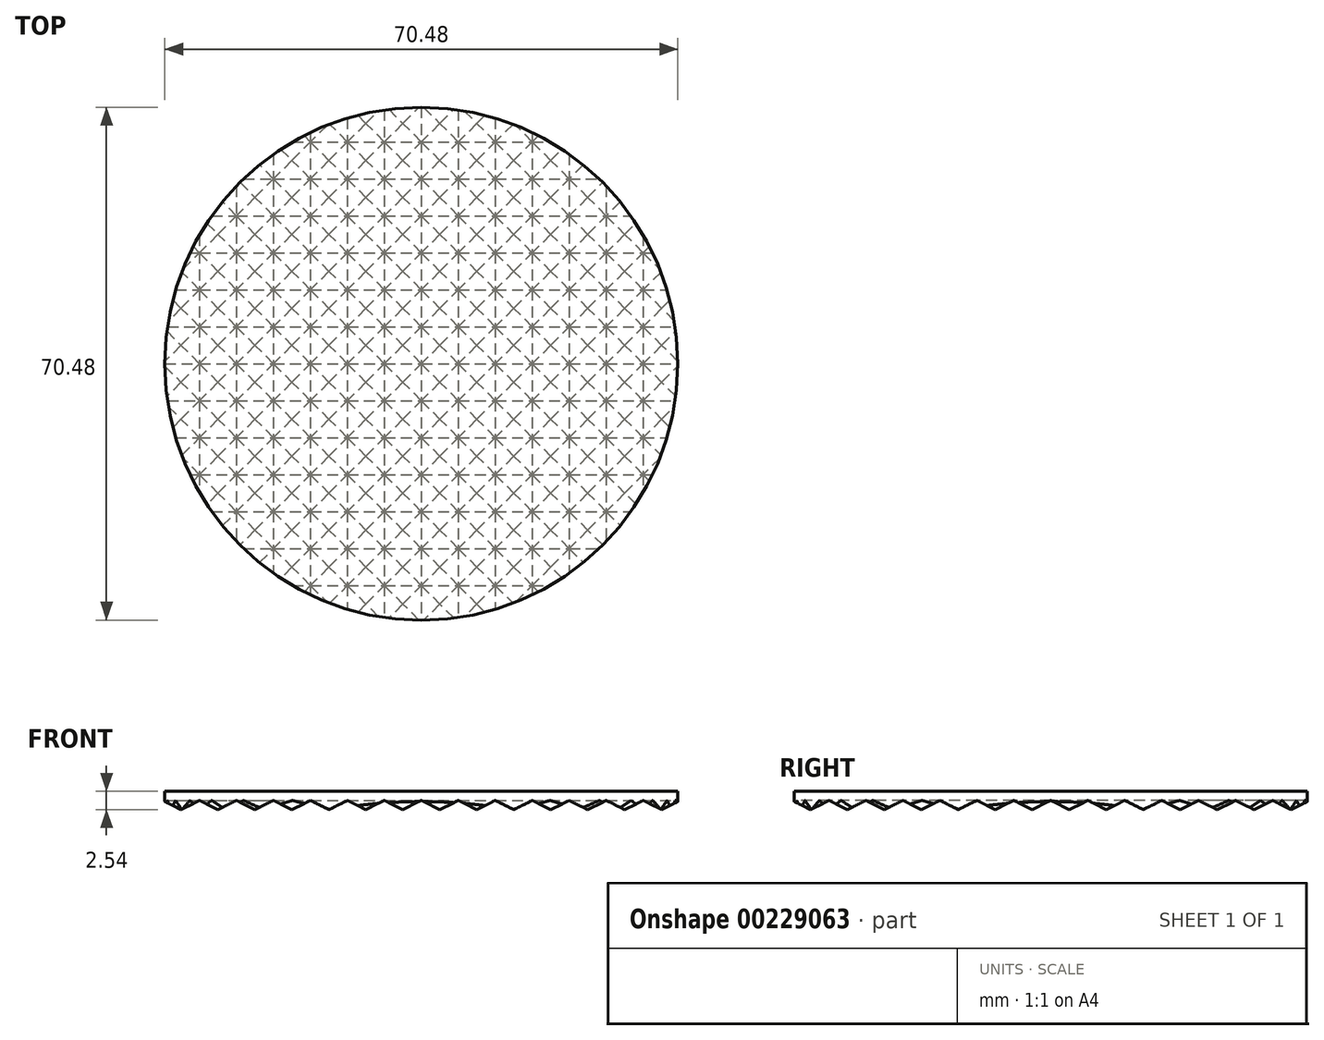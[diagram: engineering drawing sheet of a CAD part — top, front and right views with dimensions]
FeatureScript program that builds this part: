
annotation { "Feature Type Name" : "Feature", "Feature Type Description" : "" }
export const myFeature = defineFeature(function(context is Context, id is Id, definition is map)
    precondition{}
    {
        {
            var Q0;
            Q0=qCreatedBy(makeId("Top.planeOp"),FACE);
            var sketch = newSketch(context, id + "F0", { "sketchPlane" : qUnion([Q0])});
            skCircle(sketch, "E0", {"center": v(0, 0) * mm, "radius": 35.24 * mm});
            skSolve(sketch);
        }
        {
            var Q0;
            Q0 = qSketchRegion(id + "F0", true);
            extrude(context, id + "F1", {"entities" : qUnion([Q0]), "depth" : 2.54 * mm});
        }
        {
            var Q0;
            Q0=qCreatedBy(makeId("Front.planeOp"),FACE);
            var sketch = newSketch(context, id + "F2", { "sketchPlane" : qUnion([Q0])});
            skLineSegment(sketch, "E1", {"start": v(0, 0) * mm, "end": v(-2.54, 0) * mm});
            skLineSegment(sketch, "E2", {"start": v(-2.54, 0) * mm, "end": v(0, 1.27) * mm});
            skLineSegment(sketch, "E3", {"start": v(0, 1.27) * mm, "end": v(2.54, 0) * mm});
            skLineSegment(sketch, "E4", {"start": v(2.54, 0) * mm, "end": v(0, 0) * mm});
            skLineSegment(sketch, "E5.1.0.0", {"start": v(5.08, 1.27) * mm, "end": v(7.62, 0) * mm});
            skLineSegment(sketch, "E5.1.0.1", {"start": v(7.62, 0) * mm, "end": v(5.08, 0) * mm});
            skLineSegment(sketch, "E5.1.0.2", {"start": v(5.08, 0) * mm, "end": v(2.54, 0) * mm});
            skLineSegment(sketch, "E5.1.0.3", {"start": v(2.54, 0) * mm, "end": v(5.08, 1.27) * mm});
            skLineSegment(sketch, "E5.2.0.0", {"start": v(10.16, 1.27) * mm, "end": v(12.7, 0) * mm});
            skLineSegment(sketch, "E5.2.0.1", {"start": v(12.7, 0) * mm, "end": v(10.16, 0) * mm});
            skLineSegment(sketch, "E5.2.0.2", {"start": v(10.16, 0) * mm, "end": v(7.62, 0) * mm});
            skLineSegment(sketch, "E5.2.0.3", {"start": v(7.62, 0) * mm, "end": v(10.16, 1.27) * mm});
            skLineSegment(sketch, "E5.3.0.0", {"start": v(15.24, 1.27) * mm, "end": v(17.78, 0) * mm});
            skLineSegment(sketch, "E5.3.0.1", {"start": v(17.78, 0) * mm, "end": v(15.24, 0) * mm});
            skLineSegment(sketch, "E5.3.0.2", {"start": v(15.24, 0) * mm, "end": v(12.7, 0) * mm});
            skLineSegment(sketch, "E5.3.0.3", {"start": v(12.7, 0) * mm, "end": v(15.24, 1.27) * mm});
            skLineSegment(sketch, "E5.4.0.0", {"start": v(20.32, 1.27) * mm, "end": v(22.86, 0) * mm});
            skLineSegment(sketch, "E5.4.0.1", {"start": v(22.86, 0) * mm, "end": v(20.32, 0) * mm});
            skLineSegment(sketch, "E5.4.0.2", {"start": v(20.32, 0) * mm, "end": v(17.78, 0) * mm});
            skLineSegment(sketch, "E5.4.0.3", {"start": v(17.78, 0) * mm, "end": v(20.32, 1.27) * mm});
            skLineSegment(sketch, "E5.5.0.0", {"start": v(25.4, 1.27) * mm, "end": v(27.94, 0) * mm});
            skLineSegment(sketch, "E5.5.0.1", {"start": v(27.94, 0) * mm, "end": v(25.4, 0) * mm});
            skLineSegment(sketch, "E5.5.0.2", {"start": v(25.4, 0) * mm, "end": v(22.86, 0) * mm});
            skLineSegment(sketch, "E5.5.0.3", {"start": v(22.86, 0) * mm, "end": v(25.4, 1.27) * mm});
            skLineSegment(sketch, "E5.6.0.0", {"start": v(30.48, 1.27) * mm, "end": v(33.02, 0) * mm});
            skLineSegment(sketch, "E5.6.0.1", {"start": v(33.02, 0) * mm, "end": v(30.48, 0) * mm});
            skLineSegment(sketch, "E5.6.0.2", {"start": v(30.48, 0) * mm, "end": v(27.94, 0) * mm});
            skLineSegment(sketch, "E5.6.0.3", {"start": v(27.94, 0) * mm, "end": v(30.48, 1.27) * mm});
            skLineSegment(sketch, "E5.7.0.0", {"start": v(35.56, 1.27) * mm, "end": v(38.1, 0) * mm});
            skLineSegment(sketch, "E5.7.0.1", {"start": v(38.1, 0) * mm, "end": v(35.56, 0) * mm});
            skLineSegment(sketch, "E5.7.0.2", {"start": v(35.56, 0) * mm, "end": v(33.02, 0) * mm});
            skLineSegment(sketch, "E5.7.0.3", {"start": v(33.02, 0) * mm, "end": v(35.56, 1.27) * mm});
            skLineSegment(sketch, "E5.direction1", {"start": v(0, 1.27) * mm, "end": v(5.08, 1.27) * mm, "construction": true});
            skLineSegment(sketch, "E6.1.0.0", {"start": v(-2.54, 0) * mm, "end": v(-5.08, 0) * mm});
            skLineSegment(sketch, "E6.1.0.1", {"start": v(-5.08, 1.27) * mm, "end": v(-2.54, 0) * mm});
            skLineSegment(sketch, "E6.1.0.2", {"start": v(-7.62, 0) * mm, "end": v(-5.08, 1.27) * mm});
            skLineSegment(sketch, "E6.1.0.3", {"start": v(-5.08, 0) * mm, "end": v(-7.62, 0) * mm});
            skLineSegment(sketch, "E6.2.0.0", {"start": v(-7.62, 0) * mm, "end": v(-10.16, 0) * mm});
            skLineSegment(sketch, "E6.2.0.1", {"start": v(-10.16, 1.27) * mm, "end": v(-7.62, 0) * mm});
            skLineSegment(sketch, "E6.2.0.2", {"start": v(-12.7, 0) * mm, "end": v(-10.16, 1.27) * mm});
            skLineSegment(sketch, "E6.2.0.3", {"start": v(-10.16, 0) * mm, "end": v(-12.7, 0) * mm});
            skLineSegment(sketch, "E6.3.0.0", {"start": v(-12.7, 0) * mm, "end": v(-15.24, 0) * mm});
            skLineSegment(sketch, "E6.3.0.1", {"start": v(-15.24, 1.27) * mm, "end": v(-12.7, 0) * mm});
            skLineSegment(sketch, "E6.3.0.2", {"start": v(-17.78, 0) * mm, "end": v(-15.24, 1.27) * mm});
            skLineSegment(sketch, "E6.3.0.3", {"start": v(-15.24, 0) * mm, "end": v(-17.78, 0) * mm});
            skLineSegment(sketch, "E6.4.0.0", {"start": v(-17.78, 0) * mm, "end": v(-20.32, 0) * mm});
            skLineSegment(sketch, "E6.4.0.1", {"start": v(-20.32, 1.27) * mm, "end": v(-17.78, 0) * mm});
            skLineSegment(sketch, "E6.4.0.2", {"start": v(-22.86, 0) * mm, "end": v(-20.32, 1.27) * mm});
            skLineSegment(sketch, "E6.4.0.3", {"start": v(-20.32, 0) * mm, "end": v(-22.86, 0) * mm});
            skLineSegment(sketch, "E6.5.0.0", {"start": v(-22.86, 0) * mm, "end": v(-25.4, 0) * mm});
            skLineSegment(sketch, "E6.5.0.1", {"start": v(-25.4, 1.27) * mm, "end": v(-22.86, 0) * mm});
            skLineSegment(sketch, "E6.5.0.2", {"start": v(-27.94, 0) * mm, "end": v(-25.4, 1.27) * mm});
            skLineSegment(sketch, "E6.5.0.3", {"start": v(-25.4, 0) * mm, "end": v(-27.94, 0) * mm});
            skLineSegment(sketch, "E6.6.0.0", {"start": v(-27.94, 0) * mm, "end": v(-30.48, 0) * mm});
            skLineSegment(sketch, "E6.6.0.1", {"start": v(-30.48, 1.27) * mm, "end": v(-27.94, 0) * mm});
            skLineSegment(sketch, "E6.6.0.2", {"start": v(-33.02, 0) * mm, "end": v(-30.48, 1.27) * mm});
            skLineSegment(sketch, "E6.6.0.3", {"start": v(-30.48, 0) * mm, "end": v(-33.02, 0) * mm});
            skLineSegment(sketch, "E6.7.0.0", {"start": v(-33.02, 0) * mm, "end": v(-35.56, 0) * mm});
            skLineSegment(sketch, "E6.7.0.1", {"start": v(-35.56, 1.27) * mm, "end": v(-33.02, 0) * mm});
            skLineSegment(sketch, "E6.7.0.2", {"start": v(-38.1, 0) * mm, "end": v(-35.56, 1.27) * mm});
            skLineSegment(sketch, "E6.7.0.3", {"start": v(-35.56, 0) * mm, "end": v(-38.1, 0) * mm});
            skLineSegment(sketch, "E6.direction1", {"start": v(-2.54, 0) * mm, "end": v(-7.62, 0) * mm, "construction": true});
            skSolve(sketch);
        }
        {
            var Q0;
            Q0 = qSketchRegion(id + "F2", true);
            extrude(context, id + "F3", {"entities" : qUnion([Q0]), "operationType" : NewBodyOperationType.REMOVE, "oppositeDirection" : true, "depth" : 101.6 * mm, "symmetric" : true});
        }
        {
            var Q0;
            Q0=qCreatedBy(makeId("Right.planeOp"),FACE);
            var sketch = newSketch(context, id + "F4", { "sketchPlane" : qUnion([Q0])});
            skLineSegment(sketch, "E7", {"start": v(0, 0) * mm, "end": v(-2.54, 0) * mm});
            skLineSegment(sketch, "E8", {"start": v(-2.54, 0) * mm, "end": v(0, 1.27) * mm});
            skLineSegment(sketch, "E9", {"start": v(0, 1.27) * mm, "end": v(2.54, 0) * mm});
            skLineSegment(sketch, "E10", {"start": v(2.54, 0) * mm, "end": v(0, 0) * mm});
            skLineSegment(sketch, "E11.1.0.0", {"start": v(5.08, 1.27) * mm, "end": v(7.62, 0) * mm});
            skLineSegment(sketch, "E11.1.0.1", {"start": v(7.62, 0) * mm, "end": v(5.08, 0) * mm});
            skLineSegment(sketch, "E11.1.0.2", {"start": v(5.08, 0) * mm, "end": v(2.54, 0) * mm});
            skLineSegment(sketch, "E11.1.0.3", {"start": v(2.54, 0) * mm, "end": v(5.08, 1.27) * mm});
            skLineSegment(sketch, "E11.2.0.0", {"start": v(10.16, 1.27) * mm, "end": v(12.7, 0) * mm});
            skLineSegment(sketch, "E11.2.0.1", {"start": v(12.7, 0) * mm, "end": v(10.16, 0) * mm});
            skLineSegment(sketch, "E11.2.0.2", {"start": v(10.16, 0) * mm, "end": v(7.62, 0) * mm});
            skLineSegment(sketch, "E11.2.0.3", {"start": v(7.62, 0) * mm, "end": v(10.16, 1.27) * mm});
            skLineSegment(sketch, "E11.3.0.0", {"start": v(15.24, 1.27) * mm, "end": v(17.78, 0) * mm});
            skLineSegment(sketch, "E11.3.0.1", {"start": v(17.78, 0) * mm, "end": v(15.24, 0) * mm});
            skLineSegment(sketch, "E11.3.0.2", {"start": v(15.24, 0) * mm, "end": v(12.7, 0) * mm});
            skLineSegment(sketch, "E11.3.0.3", {"start": v(12.7, 0) * mm, "end": v(15.24, 1.27) * mm});
            skLineSegment(sketch, "E11.4.0.0", {"start": v(20.32, 1.27) * mm, "end": v(22.86, 0) * mm});
            skLineSegment(sketch, "E11.4.0.1", {"start": v(22.86, 0) * mm, "end": v(20.32, 0) * mm});
            skLineSegment(sketch, "E11.4.0.2", {"start": v(20.32, 0) * mm, "end": v(17.78, 0) * mm});
            skLineSegment(sketch, "E11.4.0.3", {"start": v(17.78, 0) * mm, "end": v(20.32, 1.27) * mm});
            skLineSegment(sketch, "E11.5.0.0", {"start": v(25.4, 1.27) * mm, "end": v(27.94, 0) * mm});
            skLineSegment(sketch, "E11.5.0.1", {"start": v(27.94, 0) * mm, "end": v(25.4, 0) * mm});
            skLineSegment(sketch, "E11.5.0.2", {"start": v(25.4, 0) * mm, "end": v(22.86, 0) * mm});
            skLineSegment(sketch, "E11.5.0.3", {"start": v(22.86, 0) * mm, "end": v(25.4, 1.27) * mm});
            skLineSegment(sketch, "E11.6.0.0", {"start": v(30.48, 1.27) * mm, "end": v(33.02, 0) * mm});
            skLineSegment(sketch, "E11.6.0.1", {"start": v(33.02, 0) * mm, "end": v(30.48, 0) * mm});
            skLineSegment(sketch, "E11.6.0.2", {"start": v(30.48, 0) * mm, "end": v(27.94, 0) * mm});
            skLineSegment(sketch, "E11.6.0.3", {"start": v(27.94, 0) * mm, "end": v(30.48, 1.27) * mm});
            skLineSegment(sketch, "E11.7.0.0", {"start": v(35.56, 1.27) * mm, "end": v(38.1, 0) * mm});
            skLineSegment(sketch, "E11.7.0.1", {"start": v(38.1, 0) * mm, "end": v(35.56, 0) * mm});
            skLineSegment(sketch, "E11.7.0.2", {"start": v(35.56, 0) * mm, "end": v(33.02, 0) * mm});
            skLineSegment(sketch, "E11.7.0.3", {"start": v(33.02, 0) * mm, "end": v(35.56, 1.27) * mm});
            skLineSegment(sketch, "E11.direction1", {"start": v(0, 1.27) * mm, "end": v(5.08, 1.27) * mm, "construction": true});
            skLineSegment(sketch, "E12.1.0.0", {"start": v(-2.54, 0) * mm, "end": v(-5.08, 0) * mm});
            skLineSegment(sketch, "E12.1.0.1", {"start": v(-5.08, 1.27) * mm, "end": v(-2.54, 0) * mm});
            skLineSegment(sketch, "E12.1.0.2", {"start": v(-7.62, 0) * mm, "end": v(-5.08, 1.27) * mm});
            skLineSegment(sketch, "E12.1.0.3", {"start": v(-5.08, 0) * mm, "end": v(-7.62, 0) * mm});
            skLineSegment(sketch, "E12.2.0.0", {"start": v(-7.62, 0) * mm, "end": v(-10.16, 0) * mm});
            skLineSegment(sketch, "E12.2.0.1", {"start": v(-10.16, 1.27) * mm, "end": v(-7.62, 0) * mm});
            skLineSegment(sketch, "E12.2.0.2", {"start": v(-12.7, 0) * mm, "end": v(-10.16, 1.27) * mm});
            skLineSegment(sketch, "E12.2.0.3", {"start": v(-10.16, 0) * mm, "end": v(-12.7, 0) * mm});
            skLineSegment(sketch, "E12.3.0.0", {"start": v(-12.7, 0) * mm, "end": v(-15.24, 0) * mm});
            skLineSegment(sketch, "E12.3.0.1", {"start": v(-15.24, 1.27) * mm, "end": v(-12.7, 0) * mm});
            skLineSegment(sketch, "E12.3.0.2", {"start": v(-17.78, 0) * mm, "end": v(-15.24, 1.27) * mm});
            skLineSegment(sketch, "E12.3.0.3", {"start": v(-15.24, 0) * mm, "end": v(-17.78, 0) * mm});
            skLineSegment(sketch, "E12.4.0.0", {"start": v(-17.78, 0) * mm, "end": v(-20.32, 0) * mm});
            skLineSegment(sketch, "E12.4.0.1", {"start": v(-20.32, 1.27) * mm, "end": v(-17.78, 0) * mm});
            skLineSegment(sketch, "E12.4.0.2", {"start": v(-22.86, 0) * mm, "end": v(-20.32, 1.27) * mm});
            skLineSegment(sketch, "E12.4.0.3", {"start": v(-20.32, 0) * mm, "end": v(-22.86, 0) * mm});
            skLineSegment(sketch, "E12.5.0.0", {"start": v(-22.86, 0) * mm, "end": v(-25.4, 0) * mm});
            skLineSegment(sketch, "E12.5.0.1", {"start": v(-25.4, 1.27) * mm, "end": v(-22.86, 0) * mm});
            skLineSegment(sketch, "E12.5.0.2", {"start": v(-27.94, 0) * mm, "end": v(-25.4, 1.27) * mm});
            skLineSegment(sketch, "E12.5.0.3", {"start": v(-25.4, 0) * mm, "end": v(-27.94, 0) * mm});
            skLineSegment(sketch, "E12.6.0.0", {"start": v(-27.94, 0) * mm, "end": v(-30.48, 0) * mm});
            skLineSegment(sketch, "E12.6.0.1", {"start": v(-30.48, 1.27) * mm, "end": v(-27.94, 0) * mm});
            skLineSegment(sketch, "E12.6.0.2", {"start": v(-33.02, 0) * mm, "end": v(-30.48, 1.27) * mm});
            skLineSegment(sketch, "E12.6.0.3", {"start": v(-30.48, 0) * mm, "end": v(-33.02, 0) * mm});
            skLineSegment(sketch, "E12.7.0.0", {"start": v(-33.02, 0) * mm, "end": v(-35.56, 0) * mm});
            skLineSegment(sketch, "E12.7.0.1", {"start": v(-35.56, 1.27) * mm, "end": v(-33.02, 0) * mm});
            skLineSegment(sketch, "E12.7.0.2", {"start": v(-38.1, 0) * mm, "end": v(-35.56, 1.27) * mm});
            skLineSegment(sketch, "E12.7.0.3", {"start": v(-35.56, 0) * mm, "end": v(-38.1, 0) * mm});
            skLineSegment(sketch, "E12.direction1", {"start": v(-2.54, 0) * mm, "end": v(-7.62, 0) * mm, "construction": true});
            skSolve(sketch);
        }
        {
            var Q0;
            Q0 = qSketchRegion(id + "F4", true);
            extrude(context, id + "F5", {"entities" : qUnion([Q0]), "operationType" : NewBodyOperationType.REMOVE, "oppositeDirection" : true, "depth" : 101.6 * mm, "symmetric" : true});
        }
    });
